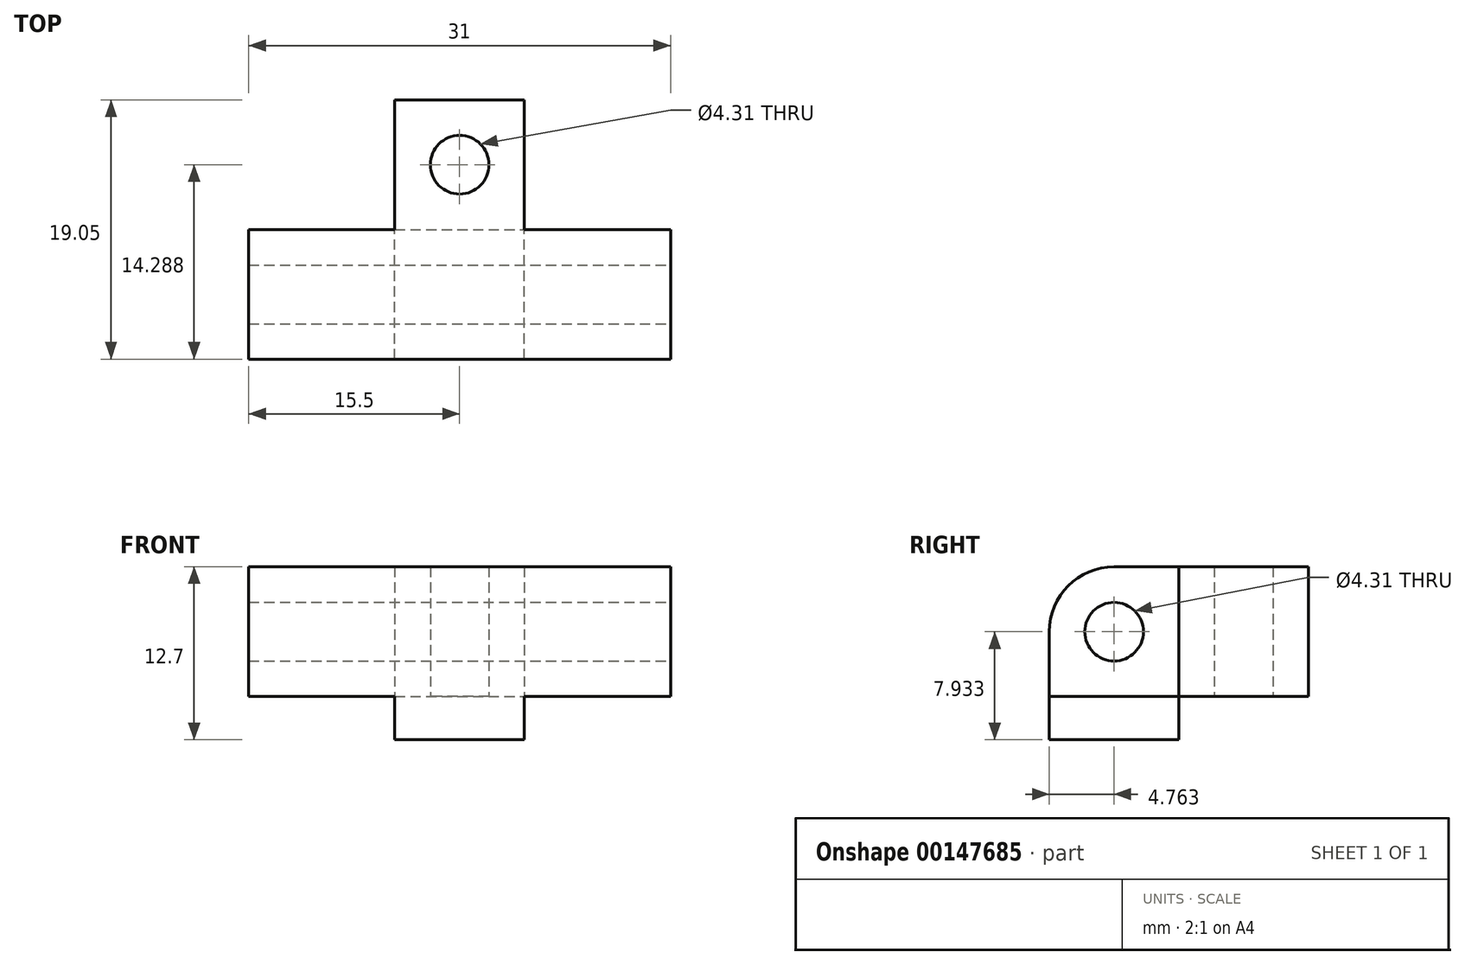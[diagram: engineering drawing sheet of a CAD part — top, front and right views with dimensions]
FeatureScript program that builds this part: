
annotation { "Feature Type Name" : "Feature", "Feature Type Description" : "" }
export const myFeature = defineFeature(function(context is Context, id is Id, definition is map)
    precondition{}
    {
        {
            var Q0;
            Q0=qCreatedBy(makeId("Top.planeOp"),FACE);
            var sketch = newSketch(context, id + "F0", { "sketchPlane" : qUnion([Q0])});
            skLineSegment(sketch, "E0.bottom", {"start": v(0, 0) * mm, "end": v(31, 0) * mm});
            skLineSegment(sketch, "E0.top", {"start": v(0, -19.05) * mm, "end": v(31, -19.05) * mm});
            skLineSegment(sketch, "E0.left", {"start": v(0, 0) * mm, "end": v(0, -19.05) * mm});
            skLineSegment(sketch, "E0.right", {"start": v(31, 0) * mm, "end": v(31, -19.05) * mm});
            skLineSegment(sketch, "E1", {"start": v(15.5, 0) * mm, "end": v(15.5, -4.76) * mm, "construction": true});
            skCircle(sketch, "E2", {"center": v(15.5, -4.76) * mm, "radius": 2.15 * mm});
            skLineSegment(sketch, "E3", {"start": v(15.5, -4.76) * mm, "end": v(0, -4.76) * mm, "construction": true});
            skSolve(sketch);
        }
        {
            var Q0;
            Q0=qSketchRegion(id+"F0",true);
            extrude(context, id + "F1", {"entities" : qUnion([Q0]), "depth" : 9.52 * mm});
        }
        {
            var Q0;
            Q0=makeQuery(id+"F1.opExtrude","SWEPT_FACE",FACE,{"disambiguationData":[OSD([sQuery(id+"F0.wireOp",EDGE,"E0.right")])]});
            var sketch = newSketch(context, id + "F2", { "sketchPlane" : qUnion([Q0])});
            skLineSegment(sketch, "E4", {"start": v(0, 4.76) * mm, "end": v(-14.29, 4.76) * mm, "construction": true});
            skCircle(sketch, "E5", {"center": v(-14.29, 4.76) * mm, "radius": 2.15 * mm});
            skSolve(sketch);
        }
        {
            var Q0;
            Q0=qSketchRegion(id+"F2",true);
            var Q1;
            Q1=makeQuery(id+"F1.opExtrude","SWEPT_FACE",FACE,{"disambiguationData":[OSD([sQuery(id+"F0.wireOp",EDGE,"E0.left")])]});
            extrude(context, id + "F3", {"entities" : qUnion([Q0]), "operationType" : NewBodyOperationType.REMOVE, "endBound" : BoundingType.UP_TO_SURFACE, "oppositeDirection" : true, "endBoundEntityFace" : qUnion([Q1]), "depth" : 25.4 * mm});
        }
        {
            var Q0;
            Q0=makeQuery(id+"F1.opExtrude","CAP_FACE",FACE,{"disambiguationData":[OSD([sQuery(id+"F0.wireOp",EDGE,"E0.bottom"),sQuery(id+"F0.wireOp",EDGE,"E0.top"),sQuery(id+"F0.wireOp",EDGE,"E0.left"),sQuery(id+"F0.wireOp",EDGE,"E0.right"),sQuery(id+"F0.wireOp",EDGE,"E2"),sQuery(id+"F0.wireOp",EDGE,"LaN50Wi6-CAFj-wKd2-t5ty-lVtg32UNv0FP")])],"isStart":true});
            var sketch = newSketch(context, id + "F4", { "sketchPlane" : qUnion([Q0])});
            skLineSegment(sketch, "E6.bottom", {"start": v(10.74, 19.05) * mm, "end": v(20.26, 19.05) * mm});
            skLineSegment(sketch, "E6.top", {"start": v(10.74, 9.52) * mm, "end": v(20.26, 9.52) * mm});
            skLineSegment(sketch, "E6.left", {"start": v(10.74, 19.05) * mm, "end": v(10.74, 9.52) * mm});
            skLineSegment(sketch, "E6.right", {"start": v(20.26, 19.05) * mm, "end": v(20.26, 9.52) * mm});
            skPoint(sketch, "E7", {"position": v(15.5, 19.05) * mm});
            skSolve(sketch);
        }
        {
            var Q0;
            Q0=qSketchRegion(id+"F4",true);
            extrude(context, id + "F5", {"entities" : qUnion([Q0]), "operationType" : NewBodyOperationType.ADD, "depth" : 3.17 * mm});
        }
        {
            var Q0;
            Q0=makeQuery(id+"F1.opExtrude","CAP_FACE",FACE,{"disambiguationData":[OSD([sQuery(id+"F0.wireOp",EDGE,"E0.bottom"),sQuery(id+"F0.wireOp",EDGE,"E0.top"),sQuery(id+"F0.wireOp",EDGE,"E0.left"),sQuery(id+"F0.wireOp",EDGE,"E0.right"),sQuery(id+"F0.wireOp",EDGE,"E2")])],"isStart":true});
            var sketch = newSketch(context, id + "F6", { "sketchPlane" : qUnion([Q0])});
            skLineSegment(sketch, "E8.bottom", {"start": v(20.26, 9.52) * mm, "end": v(31, 9.52) * mm});
            skLineSegment(sketch, "E8.top", {"start": v(20.26, 0) * mm, "end": v(31, 0) * mm});
            skLineSegment(sketch, "E8.left", {"start": v(20.26, 9.52) * mm, "end": v(20.26, 0) * mm});
            skLineSegment(sketch, "E8.right", {"start": v(31, 9.52) * mm, "end": v(31, 0) * mm});
            skLineSegment(sketch, "E9.bottom", {"start": v(10.74, 9.52) * mm, "end": v(0, 9.52) * mm});
            skLineSegment(sketch, "E9.top", {"start": v(10.74, 0) * mm, "end": v(0, 0) * mm});
            skLineSegment(sketch, "E9.left", {"start": v(10.74, 9.52) * mm, "end": v(10.74, 0) * mm});
            skLineSegment(sketch, "E9.right", {"start": v(0, 9.52) * mm, "end": v(0, 0) * mm});
            skSolve(sketch);
        }
        {
            var Q0;
            Q0=qSketchRegion(id+"F6",true);
            var Q1;
            Q1=makeQuery(id+"F1.opExtrude","CAP_FACE",FACE,{"disambiguationData":[OSD([sQuery(id+"F0.wireOp",EDGE,"E0.bottom"),sQuery(id+"F0.wireOp",EDGE,"E0.top"),sQuery(id+"F0.wireOp",EDGE,"E0.left"),sQuery(id+"F0.wireOp",EDGE,"E0.right"),sQuery(id+"F0.wireOp",EDGE,"E2")])],"isStart":false});
            extrude(context, id + "F7", {"entities" : qUnion([Q0]), "operationType" : NewBodyOperationType.REMOVE, "endBound" : BoundingType.UP_TO_SURFACE, "oppositeDirection" : true, "endBoundEntityFace" : qUnion([Q1]), "depth" : 25.4 * mm});
        }
        {
            var Q0;
            Q0=makeQuery(id+"F1.opExtrude","CAP_EDGE",EDGE,{"disambiguationData":[OSD([sQuery(id+"F0.wireOp",EDGE,"E0.top")])],"isStart":false});
            var Q1;
            Q1=makeQuery(id+"F7.boolean.opBoolean","COPY",EDGE,{"derivedFrom":makeQuery(id+"F7.opExtrude","TWEAK_EDGE",EDGE,{"derivedFrom":[makeQuery(id+"F1.opExtrude","CAP_FACE",FACE,{"disambiguationData":[OSD([sQuery(id+"F0.wireOp",EDGE,"E0.bottom"),sQuery(id+"F0.wireOp",EDGE,"E0.top"),sQuery(id+"F0.wireOp",EDGE,"E0.left"),sQuery(id+"F0.wireOp",EDGE,"E0.right"),sQuery(id+"F0.wireOp",EDGE,"E2")])],"isStart":false}),makeQuery(id+"F6.imprint","IMPRINT",EDGE,{"derivedFrom":sQuery(id+"F6.wireOp",EDGE,"E8.bottom")})]})});
            var Q2;
            Q2=makeQuery(id+"F7.boolean.opBoolean","COPY",EDGE,{"derivedFrom":makeQuery(id+"F7.opExtrude","TWEAK_EDGE",EDGE,{"derivedFrom":[makeQuery(id+"F1.opExtrude","CAP_FACE",FACE,{"disambiguationData":[OSD([sQuery(id+"F0.wireOp",EDGE,"E0.bottom"),sQuery(id+"F0.wireOp",EDGE,"E0.top"),sQuery(id+"F0.wireOp",EDGE,"E0.left"),sQuery(id+"F0.wireOp",EDGE,"E0.right"),sQuery(id+"F0.wireOp",EDGE,"E2")])],"isStart":false}),makeQuery(id+"F6.imprint","IMPRINT",EDGE,{"derivedFrom":sQuery(id+"F6.wireOp",EDGE,"E9.bottom")})]})});
            fillet(context, id + "F8", {"entities" : qUnion([Q0, Q1, Q2]), "radius" : 4.76 * mm, "tangentPropagation" : true, "allowEdgeOverflow" : false});
        }
    });
